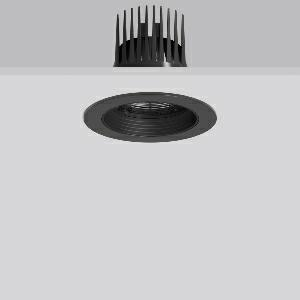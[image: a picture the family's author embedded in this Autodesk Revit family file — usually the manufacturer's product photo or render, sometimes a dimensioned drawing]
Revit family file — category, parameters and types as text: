
# Revit family: heledon_maxi_e_901760_003_3_76_f691
name_source: partatom
category: Lighting Fixtures
units: mm (PartAtom-declared; Revit-internal decimal feet)

## family parameters
Cut with Voids When Loaded = No
Host = Face
Light Source = No
Part Type = Normal
Room Calculation Point = No
Round Connector Dimension = Use Diameter
Shared = No

## types (1)
- HELEDON maxi E (1 x LED Modul 935, 2900 lm, 3500)
    Apparent Load = 25 VA
    Approval mark = CE
    CIE Flux Codes = 97 100 100 100 100
    Color Rendering = 92
    Color Temperature = 3500
    Default Elevation = 1800 mm
    Description = Series: HELEDON maxi
Round recessed downlight. Housing: die-cast aluminium, powder-coated. Black plastic ring and recessed LED to prevent glare from the side. Optical assembly with lens made of plastic (polycarbonate) for the best homogeneous light distribution - can be changed without tools. Best colour rendering index Ra>90. Suitable for Recessed ceiling mounting. Installation without tools thanks to spring fastening system. Including separate LED converter with connecting cable 600 mm.High quality converter without flickering and stroboscopic effect. Through-wiring box (5 pole) available as accessory. The following accessories can be mounted without use of tools: interchangeable lenses, decorative glasses, honeycomb louvre, clear and frosted diffusers, white interchangeable plastic ring. 
Colour: deep black, matt (RAL 9005)
Diameter: 162 mm
Height: 3 mm
Cut-out diameter: 152 mm
Recess height: 200 mm
Luminaire: recess height: 135 mm
Lamp: LED
Socket: without socket
Colour temperature: 3500K
Colour rendering index (CRI): 92
System power: 25 W
Rated luminous flux: 2900 lm
Luminous efficiency: 116 lm/W
Control gear: Converter, dimmable, DALI
Protection class: II
Type of protection: IP 20
    Height = 0 mm  [stored 0 ft]
    Lamp = 1 x LED Modul 935
    Lamp Light Flux = 2900 lm
    Lamp count = 1
    Length = 162 mm
    Lifetime = 50000 h
    Luminous efficacy = 116 lm/W
    Manufacturer = RZB
    ModVariant = No
    Model = 901760.003.3.76
    Mounting Place = Ceiling
    Mounting Type = Recessed
    Number of Poles = 1
    OnlyDefault = Yes
    Power Factor = 1
    Product Name = HELEDON maxi E
    Product group = Recessed downlights
    ProductGroupID = 402
    Protection Class = Protection class II
    Protection Degree = IP 20
    RLX_Detail_Level = 1
    RLX_Emergency_Light_Flux = 0 lm
    RLX_Emergency_Type = 0
    RLX_Emergency_Type_DB = No
    RlxData = <blob elided: 120453 chars, md5=851d0b7a>
    Socket = socket
    Standby Power = 0 W
    System Light Flux = 2900 lm
    System Power = 25 W
    Type Comments = Product without accessories
    Type Image = 901663.003.jpg
    URL = http://relux.com
    VarID = ---
    Voltage = 230 V
    Voltage Range = 220-240 V
    Weight = 0.00 kg
    Width = 0 mm  [stored 0 ft]

note: [stored X ft] marks values corroborated as IEEE doubles in the binary element streams (Revit-internal decimal feet)

## geometry (parser evidence)
native form markers: Blend x4, Sweep x11
no freeform markers — native parametric forms only
